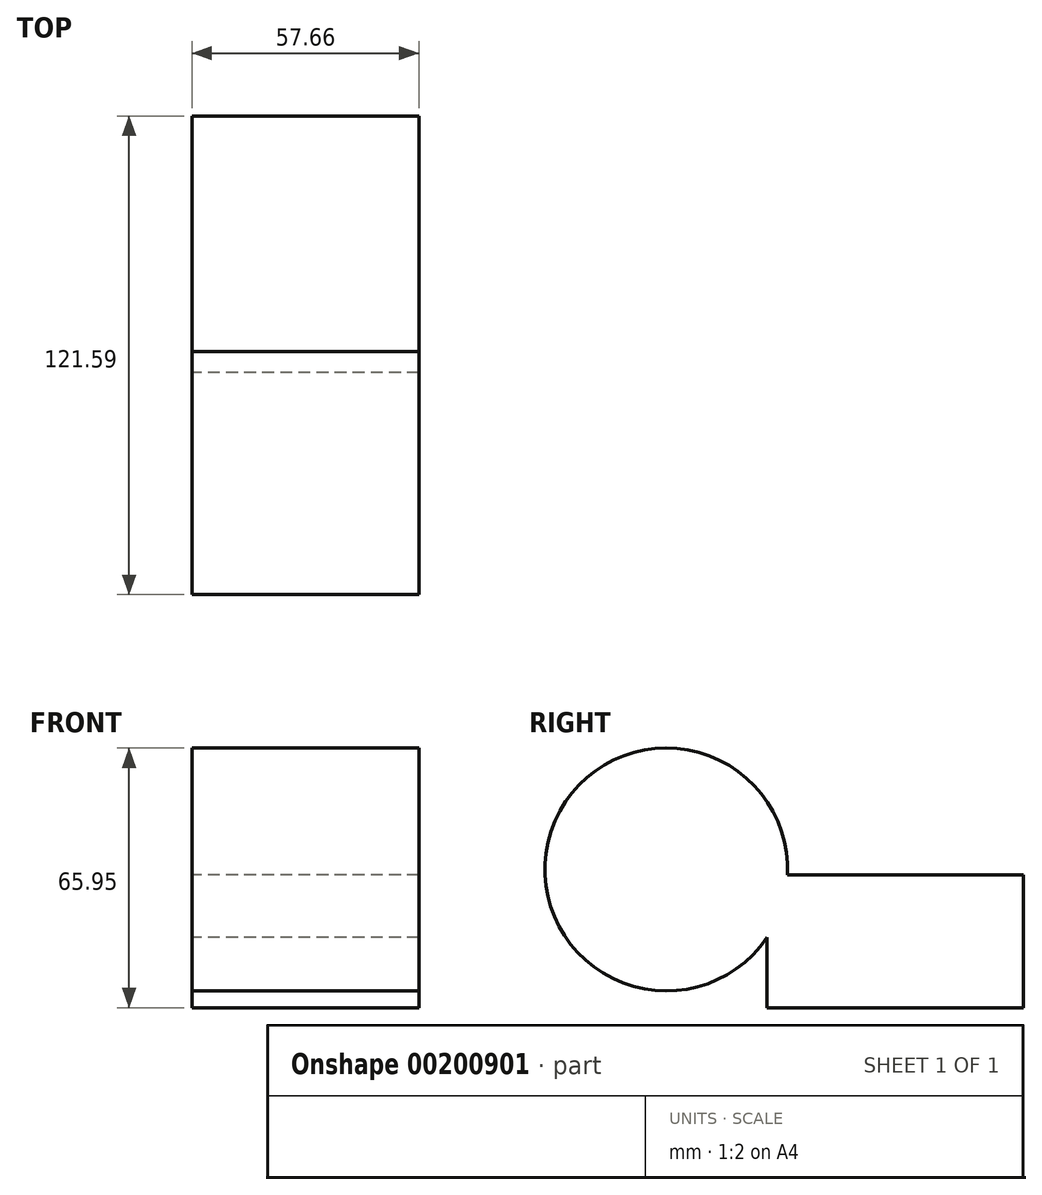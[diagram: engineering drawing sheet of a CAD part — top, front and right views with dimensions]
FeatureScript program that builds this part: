
annotation { "Feature Type Name" : "Feature", "Feature Type Description" : "" }
export const myFeature = defineFeature(function(context is Context, id is Id, definition is map)
    precondition{}
    {
        {
            var Q0;
            Q0=qCreatedBy(makeId("Right.planeOp"),FACE);
            var sketch = newSketch(context, id + "F0", { "sketchPlane" : qUnion([Q0])});
            skLineSegment(sketch, "E0.bottom", {"start": v(-53.9, 39.08) * mm, "end": v(11.27, 39.08) * mm});
            skLineSegment(sketch, "E0.top", {"start": v(-53.9, 5.31) * mm, "end": v(11.27, 5.31) * mm});
            skLineSegment(sketch, "E0.left", {"start": v(-53.9, 39.08) * mm, "end": v(-53.9, 5.31) * mm});
            skLineSegment(sketch, "E0.right", {"start": v(11.27, 39.08) * mm, "end": v(11.27, 5.31) * mm});
            skCircle(sketch, "E1", {"center": v(-79.46, 40.4) * mm, "radius": 30.86 * mm});
            skSolve(sketch);
        }
        {
            var Q0;
            Q0 = qSketchRegion(id + "F0", true);
            extrude(context, id + "F1", {"entities" : qUnion([Q0]), "depth" : 32.26 * mm});
        }
        {
            var Q0;
            {var subQ0=sQuery(id+"F0.wireOp",EDGE,"E0.left");var subQ1=sQuery(id+"F0.wireOp",EDGE,"E0.bottom");var subQ2=makeQuery(id+"F0.imprint","INTERSECT",VERTEX,{"derivedFrom":[subQ1,subQ0]});Q0=makeQuery(id+"F0.imprint","IMPRINT",FACE,{"disambiguationData":[TD([[makeQuery(id+"F0.imprint","IMPRINT",EDGE,{"disambiguationData":[TD([[subQ2,-1.0]])],"derivedFrom":subQ1}),1.0]])]});}
            var Q1;
            Q1=makeQuery(id+"F1.opExtrude","CAP_FACE",FACE,{"disambiguationData":[OSD([sQuery(id+"F0.wireOp",EDGE,"E0.bottom"),sQuery(id+"F0.wireOp",EDGE,"E0.top"),sQuery(id+"F0.wireOp",EDGE,"E0.left"),sQuery(id+"F0.wireOp",EDGE,"E0.right"),sQuery(id+"F0.wireOp",EDGE,"E1")])],"isStart":false});
            extrude(context, id + "F2", {"entities" : qUnion([Q0, Q1]), "operationType" : NewBodyOperationType.ADD, "depth" : 25.4 * mm});
        }
    });
